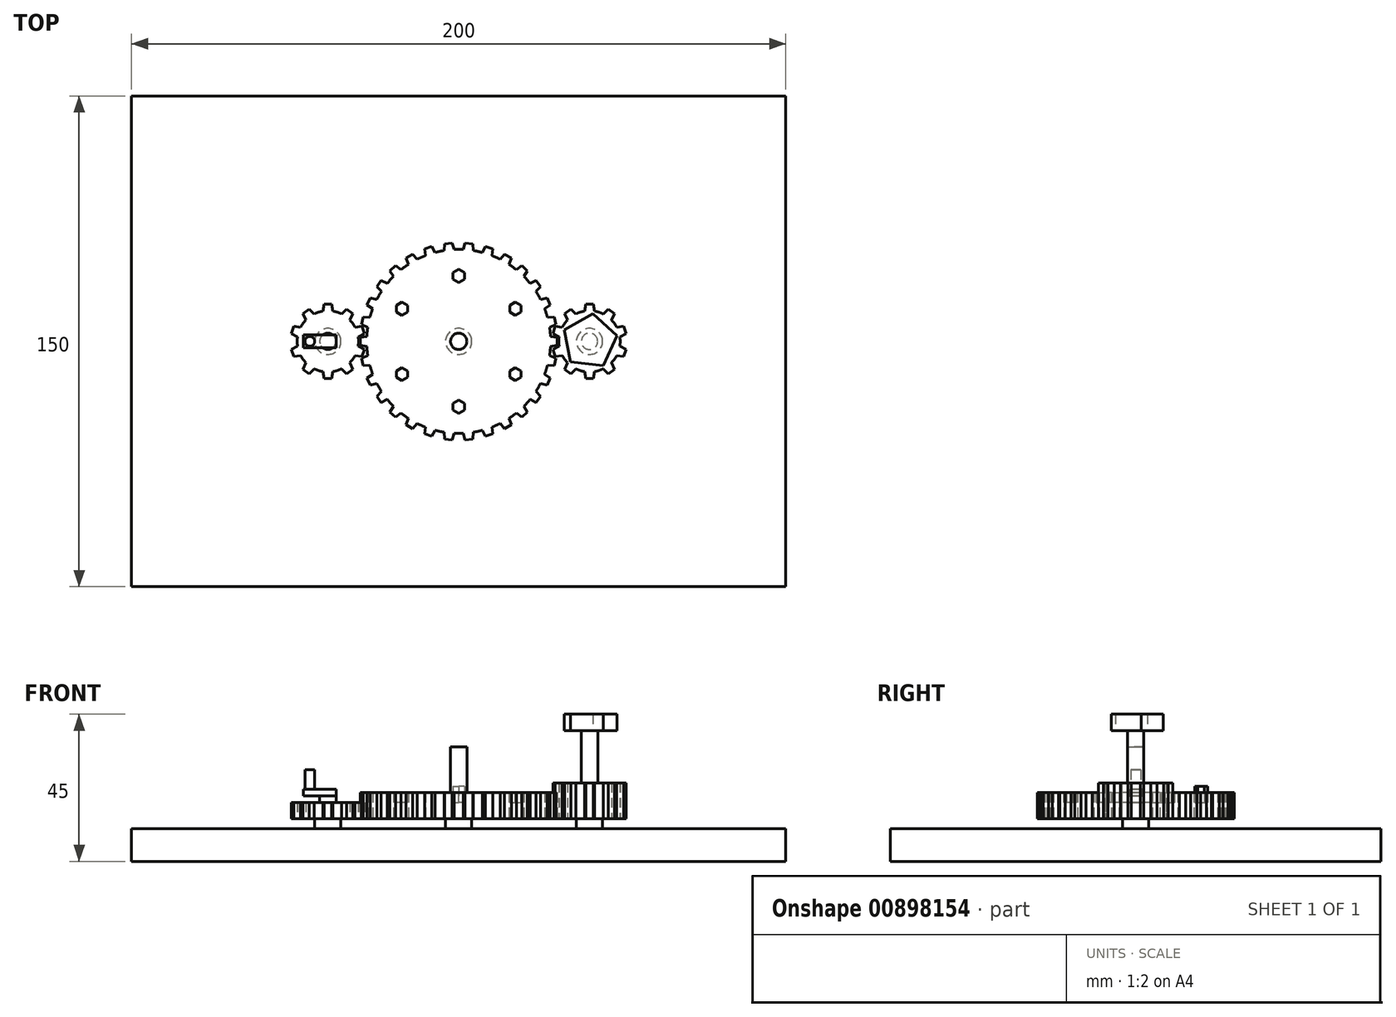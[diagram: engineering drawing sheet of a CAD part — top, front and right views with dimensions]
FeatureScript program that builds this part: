
annotation { "Feature Type Name" : "Feature", "Feature Type Description" : "" }
export const myFeature = defineFeature(function(context is Context, id is Id, definition is map)
    precondition{}
    {
        {
            var Q0;
            Q0=qCreatedBy(makeId("Top.planeOp"),FACE);
            var sketch = newSketch(context, id + "F0", { "sketchPlane" : qUnion([Q0])});
            skLineSegment(sketch, "E0.bottom", {"start": v(-100, 75) * mm, "end": v(100, 75) * mm});
            skLineSegment(sketch, "E0.top", {"start": v(-100, -75) * mm, "end": v(100, -75) * mm});
            skLineSegment(sketch, "E0.left", {"start": v(-100, 75) * mm, "end": v(-100, -75) * mm});
            skLineSegment(sketch, "E0.right", {"start": v(100, 75) * mm, "end": v(100, -75) * mm});
            skPoint(sketch, "E0.middle", {"position": v(0, 0) * mm});
            skSolve(sketch);
        }
        {
            var Q0;
            Q0 = qSketchRegion(id + "F0", true);
            extrude(context, id + "F1", {"entities" : qUnion([Q0]), "depth" : 10 * mm, "offsetDistance" : 25 * mm});
        }
        {
            var Q0;
            Q0=makeQuery(id+"F1.opExtrude","CAP_FACE",FACE,{"disambiguationData":[OSD([sQuery(id+"F0.wireOp",EDGE,"E0.bottom"),sQuery(id+"F0.wireOp",EDGE,"E0.top"),sQuery(id+"F0.wireOp",EDGE,"E0.left"),sQuery(id+"F0.wireOp",EDGE,"E0.right")])],"isStart":false});
            var sketch = newSketch(context, id + "F2", { "sketchPlane" : qUnion([Q0])});
            skCircle(sketch, "E1", {"center": v(0, 0) * mm, "radius": 4 * mm});
            skCircle(sketch, "E2", {"center": v(0, 0) * mm, "radius": 2.5 * mm});
            skCircle(sketch, "E3", {"center": v(-40, 0) * mm, "radius": 4 * mm});
            skCircle(sketch, "E4", {"center": v(-40, 0) * mm, "radius": 2.5 * mm});
            skCircle(sketch, "E5", {"center": v(40, 0) * mm, "radius": 2.5 * mm});
            skCircle(sketch, "E6", {"center": v(40, 0) * mm, "radius": 4 * mm});
            skSolve(sketch);
        }
        {
            var Q0;
            Q0 = qSketchRegion(id + "F2", true);
            extrude(context, id + "F3", {"entities" : qUnion([Q0]), "operationType" : NewBodyOperationType.ADD, "depth" : 3 * mm, "offsetDistance" : 25 * mm});
        }
        {
            var Q0;
            Q0=makeQuery(id+"F3.boolean.opBoolean","SPLIT",FACE,{"disambiguationData":[TD([makeQuery(id+"F3.opExtrude","SWEPT_FACE",FACE,{"disambiguationData":[OSD([sQuery(id+"F2.wireOp",EDGE,"E4")])]})])],"derivedFrom":makeQuery(id+"F1.opExtrude","CAP_FACE",FACE,{"disambiguationData":[OSD([sQuery(id+"F0.wireOp",EDGE,"E0.bottom"),sQuery(id+"F0.wireOp",EDGE,"E0.top"),sQuery(id+"F0.wireOp",EDGE,"E0.left"),sQuery(id+"F0.wireOp",EDGE,"E0.right")])],"isStart":false})});
            extrude(context, id + "F4", {"entities" : qUnion([Q0]), "depth" : 10 * mm, "offsetDistance" : 25 * mm});
        }
        {
            var Q0;
            Q0=makeQuery(id+"F3.opExtrude","CAP_FACE",FACE,{"disambiguationData":[OSD([sQuery(id+"F2.wireOp",EDGE,"E3"),sQuery(id+"F2.wireOp",EDGE,"E4")])],"isStart":false});
            var sketch = newSketch(context, id + "F5", { "sketchPlane" : qUnion([Q0])});
            skCircle(sketch, "E7", {"center": v(-40, 0) * mm, "radius": 9.38 * mm});
            skLineSegment(sketch, "E8", {"start": v(-40, 0) * mm, "end": v(-40, 9.38) * mm, "construction": true});
            skLineSegment(sketch, "E9", {"start": v(-41.55, 9.25) * mm, "end": v(-41.18, 11.37) * mm});
            skLineSegment(sketch, "E10", {"start": v(-41.18, 11.38) * mm, "end": v(-40, 11.38) * mm});
            skLineSegment(sketch, "E11.MirrorCS", {"start": v(-38.82, 11.38) * mm, "end": v(-40, 11.38) * mm});
            skLineSegment(sketch, "E12.MirrorCS", {"start": v(-38.45, 9.25) * mm, "end": v(-38.82, 11.37) * mm});
            skLineSegment(sketch, "E13.1.0", {"start": v(-46.7, 6.57) * mm, "end": v(-47.64, 8.51) * mm});
            skLineSegment(sketch, "E13.1.1", {"start": v(-47.64, 8.51) * mm, "end": v(-46.69, 9.2) * mm});
            skLineSegment(sketch, "E13.1.2", {"start": v(-45.73, 9.9) * mm, "end": v(-46.69, 9.2) * mm});
            skLineSegment(sketch, "E13.1.3", {"start": v(-44.18, 8.4) * mm, "end": v(-45.73, 9.9) * mm});
            skLineSegment(sketch, "E13.2.0", {"start": v(-49.27, 1.38) * mm, "end": v(-51.18, 2.4) * mm});
            skLineSegment(sketch, "E13.2.1", {"start": v(-51.18, 2.4) * mm, "end": v(-50.82, 3.52) * mm});
            skLineSegment(sketch, "E13.2.2", {"start": v(-50.45, 4.64) * mm, "end": v(-50.82, 3.52) * mm});
            skLineSegment(sketch, "E13.2.3", {"start": v(-48.31, 4.33) * mm, "end": v(-50.45, 4.64) * mm});
            skLineSegment(sketch, "E14.1.3.0", {"start": v(-48.31, -4.33) * mm, "end": v(-50.45, -4.64) * mm});
            skLineSegment(sketch, "E14.3.3.0", {"start": v(-50.45, -4.64) * mm, "end": v(-50.82, -3.52) * mm});
            skLineSegment(sketch, "E14.6.3.0", {"start": v(-51.18, -2.4) * mm, "end": v(-50.82, -3.52) * mm});
            skLineSegment(sketch, "E14.9.3.0", {"start": v(-49.27, -1.38) * mm, "end": v(-51.18, -2.4) * mm});
            skLineSegment(sketch, "E14.1.4.0", {"start": v(-44.18, -8.4) * mm, "end": v(-45.73, -9.9) * mm});
            skLineSegment(sketch, "E14.3.4.0", {"start": v(-45.73, -9.9) * mm, "end": v(-46.69, -9.2) * mm});
            skLineSegment(sketch, "E14.6.4.0", {"start": v(-47.64, -8.51) * mm, "end": v(-46.69, -9.2) * mm});
            skLineSegment(sketch, "E14.9.4.0", {"start": v(-46.7, -6.57) * mm, "end": v(-47.64, -8.51) * mm});
            skLineSegment(sketch, "E14.1.5.0", {"start": v(-38.45, -9.25) * mm, "end": v(-38.82, -11.38) * mm});
            skLineSegment(sketch, "E14.3.5.0", {"start": v(-38.82, -11.38) * mm, "end": v(-40, -11.38) * mm});
            skLineSegment(sketch, "E14.6.5.0", {"start": v(-41.18, -11.38) * mm, "end": v(-40, -11.38) * mm});
            skLineSegment(sketch, "E14.9.5.0", {"start": v(-41.55, -9.25) * mm, "end": v(-41.18, -11.38) * mm});
            skLineSegment(sketch, "E14.1.6.0", {"start": v(-33.3, -6.57) * mm, "end": v(-32.36, -8.51) * mm});
            skLineSegment(sketch, "E14.3.6.0", {"start": v(-32.36, -8.51) * mm, "end": v(-33.31, -9.2) * mm});
            skLineSegment(sketch, "E14.6.6.0", {"start": v(-34.27, -9.9) * mm, "end": v(-33.31, -9.2) * mm});
            skLineSegment(sketch, "E14.9.6.0", {"start": v(-35.82, -8.4) * mm, "end": v(-34.27, -9.9) * mm});
            skLineSegment(sketch, "E15.1.7.0", {"start": v(-30.73, -1.38) * mm, "end": v(-28.82, -2.4) * mm});
            skLineSegment(sketch, "E15.3.7.0", {"start": v(-28.82, -2.4) * mm, "end": v(-29.18, -3.52) * mm});
            skLineSegment(sketch, "E15.6.7.0", {"start": v(-29.55, -4.64) * mm, "end": v(-29.18, -3.52) * mm});
            skLineSegment(sketch, "E15.9.7.0", {"start": v(-31.69, -4.33) * mm, "end": v(-29.55, -4.64) * mm});
            skLineSegment(sketch, "E15.1.8.0", {"start": v(-31.69, 4.33) * mm, "end": v(-29.55, 4.64) * mm});
            skLineSegment(sketch, "E15.3.8.0", {"start": v(-29.55, 4.64) * mm, "end": v(-29.18, 3.52) * mm});
            skLineSegment(sketch, "E15.6.8.0", {"start": v(-28.82, 2.4) * mm, "end": v(-29.18, 3.52) * mm});
            skLineSegment(sketch, "E15.9.8.0", {"start": v(-30.73, 1.38) * mm, "end": v(-28.82, 2.4) * mm});
            skLineSegment(sketch, "E16.1.9.0", {"start": v(-35.82, 8.4) * mm, "end": v(-34.27, 9.9) * mm});
            skLineSegment(sketch, "E16.3.9.0", {"start": v(-34.27, 9.9) * mm, "end": v(-33.31, 9.2) * mm});
            skLineSegment(sketch, "E16.6.9.0", {"start": v(-32.36, 8.51) * mm, "end": v(-33.31, 9.2) * mm});
            skLineSegment(sketch, "E16.9.9.0", {"start": v(-33.3, 6.57) * mm, "end": v(-32.36, 8.51) * mm});
            skSolve(sketch);
        }
        {
            var Q0;
            Q0 = qSketchRegion(id + "F5", true);
            extrude(context, id + "F6", {"entities" : qUnion([Q0]), "operationType" : NewBodyOperationType.ADD, "depth" : 5 * mm, "offsetDistance" : 25 * mm});
        }
        {
            var Q0;
            Q0=makeQuery(id+"F3.boolean.opBoolean","SPLIT",FACE,{"disambiguationData":[TD([makeQuery(id+"F3.opExtrude","SWEPT_FACE",FACE,{"disambiguationData":[OSD([sQuery(id+"F2.wireOp",EDGE,"E2")])]})])],"derivedFrom":makeQuery(id+"F1.opExtrude","CAP_FACE",FACE,{"disambiguationData":[OSD([sQuery(id+"F0.wireOp",EDGE,"E0.bottom"),sQuery(id+"F0.wireOp",EDGE,"E0.top"),sQuery(id+"F0.wireOp",EDGE,"E0.left"),sQuery(id+"F0.wireOp",EDGE,"E0.right")])],"isStart":false})});
            extrude(context, id + "F7", {"entities" : qUnion([Q0]), "depth" : 25 * mm, "offsetDistance" : 25 * mm});
        }
        {
            var Q0;
            Q0=makeQuery(id+"F3.boolean.opBoolean","SPLIT",FACE,{"disambiguationData":[TD([makeQuery(id+"F3.opExtrude","SWEPT_FACE",FACE,{"disambiguationData":[OSD([sQuery(id+"F2.wireOp",EDGE,"E5")])]})])],"derivedFrom":makeQuery(id+"F1.opExtrude","CAP_FACE",FACE,{"disambiguationData":[OSD([sQuery(id+"F0.wireOp",EDGE,"E0.bottom"),sQuery(id+"F0.wireOp",EDGE,"E0.top"),sQuery(id+"F0.wireOp",EDGE,"E0.left"),sQuery(id+"F0.wireOp",EDGE,"E0.right")])],"isStart":false})});
            extrude(context, id + "F8", {"entities" : qUnion([Q0]), "depth" : 30 * mm, "offsetDistance" : 25 * mm});
        }
        {
            var Q0;
            Q0=makeQuery(id+"F3.opExtrude","CAP_FACE",FACE,{"disambiguationData":[OSD([sQuery(id+"F2.wireOp",EDGE,"E5"),sQuery(id+"F2.wireOp",EDGE,"E6")])],"isStart":false});
            var sketch = newSketch(context, id + "F9", { "sketchPlane" : qUnion([Q0])});
            skCircle(sketch, "E17", {"center": v(40, 0) * mm, "radius": 9.38 * mm});
            skLineSegment(sketch, "E18", {"start": v(40, 0) * mm, "end": v(40, 9.38) * mm, "construction": true});
            skLineSegment(sketch, "E19", {"start": v(38.45, 9.25) * mm, "end": v(38.82, 11.37) * mm});
            skLineSegment(sketch, "E20", {"start": v(38.82, 11.38) * mm, "end": v(40, 11.38) * mm});
            skLineSegment(sketch, "E21.MirrorCS", {"start": v(41.18, 11.38) * mm, "end": v(40, 11.38) * mm});
            skLineSegment(sketch, "E22.MirrorCS", {"start": v(41.55, 9.25) * mm, "end": v(41.18, 11.37) * mm});
            skLineSegment(sketch, "E23.1.0", {"start": v(33.3, 6.57) * mm, "end": v(32.36, 8.51) * mm});
            skLineSegment(sketch, "E23.1.1", {"start": v(32.36, 8.51) * mm, "end": v(33.31, 9.2) * mm});
            skLineSegment(sketch, "E23.1.2", {"start": v(34.27, 9.9) * mm, "end": v(33.31, 9.2) * mm});
            skLineSegment(sketch, "E23.1.3", {"start": v(35.82, 8.4) * mm, "end": v(34.27, 9.9) * mm});
            skLineSegment(sketch, "E23.2.0", {"start": v(30.73, 1.38) * mm, "end": v(28.82, 2.4) * mm});
            skLineSegment(sketch, "E23.2.1", {"start": v(28.82, 2.4) * mm, "end": v(29.18, 3.52) * mm});
            skLineSegment(sketch, "E23.2.2", {"start": v(29.55, 4.64) * mm, "end": v(29.18, 3.52) * mm});
            skLineSegment(sketch, "E23.2.3", {"start": v(31.69, 4.33) * mm, "end": v(29.55, 4.64) * mm});
            skLineSegment(sketch, "E24.1.3.0", {"start": v(31.69, -4.33) * mm, "end": v(29.55, -4.64) * mm});
            skLineSegment(sketch, "E24.3.3.0", {"start": v(29.55, -4.64) * mm, "end": v(29.18, -3.52) * mm});
            skLineSegment(sketch, "E24.6.3.0", {"start": v(28.82, -2.4) * mm, "end": v(29.18, -3.52) * mm});
            skLineSegment(sketch, "E24.9.3.0", {"start": v(30.73, -1.38) * mm, "end": v(28.82, -2.4) * mm});
            skLineSegment(sketch, "E24.1.4.0", {"start": v(35.82, -8.4) * mm, "end": v(34.27, -9.9) * mm});
            skLineSegment(sketch, "E24.3.4.0", {"start": v(34.27, -9.9) * mm, "end": v(33.31, -9.2) * mm});
            skLineSegment(sketch, "E24.6.4.0", {"start": v(32.36, -8.51) * mm, "end": v(33.31, -9.2) * mm});
            skLineSegment(sketch, "E24.9.4.0", {"start": v(33.3, -6.57) * mm, "end": v(32.36, -8.51) * mm});
            skLineSegment(sketch, "E24.1.5.0", {"start": v(41.55, -9.25) * mm, "end": v(41.18, -11.38) * mm});
            skLineSegment(sketch, "E24.3.5.0", {"start": v(41.18, -11.38) * mm, "end": v(40, -11.38) * mm});
            skLineSegment(sketch, "E24.6.5.0", {"start": v(38.82, -11.38) * mm, "end": v(40, -11.38) * mm});
            skLineSegment(sketch, "E24.9.5.0", {"start": v(38.45, -9.25) * mm, "end": v(38.82, -11.38) * mm});
            skLineSegment(sketch, "E24.1.6.0", {"start": v(46.7, -6.57) * mm, "end": v(47.64, -8.51) * mm});
            skLineSegment(sketch, "E24.3.6.0", {"start": v(47.64, -8.51) * mm, "end": v(46.69, -9.2) * mm});
            skLineSegment(sketch, "E24.6.6.0", {"start": v(45.73, -9.9) * mm, "end": v(46.69, -9.2) * mm});
            skLineSegment(sketch, "E24.9.6.0", {"start": v(44.18, -8.4) * mm, "end": v(45.73, -9.9) * mm});
            skLineSegment(sketch, "E24.1.7.0", {"start": v(49.27, -1.38) * mm, "end": v(51.18, -2.4) * mm});
            skLineSegment(sketch, "E24.3.7.0", {"start": v(51.18, -2.4) * mm, "end": v(50.82, -3.52) * mm});
            skLineSegment(sketch, "E24.6.7.0", {"start": v(50.45, -4.64) * mm, "end": v(50.82, -3.52) * mm});
            skLineSegment(sketch, "E24.9.7.0", {"start": v(48.31, -4.33) * mm, "end": v(50.45, -4.64) * mm});
            skLineSegment(sketch, "E24.1.8.0", {"start": v(48.31, 4.33) * mm, "end": v(50.45, 4.64) * mm});
            skLineSegment(sketch, "E24.3.8.0", {"start": v(50.45, 4.64) * mm, "end": v(50.82, 3.52) * mm});
            skLineSegment(sketch, "E24.6.8.0", {"start": v(51.18, 2.4) * mm, "end": v(50.82, 3.52) * mm});
            skLineSegment(sketch, "E24.9.8.0", {"start": v(49.27, 1.38) * mm, "end": v(51.18, 2.4) * mm});
            skLineSegment(sketch, "E25.1.9.0", {"start": v(44.18, 8.4) * mm, "end": v(45.73, 9.9) * mm});
            skLineSegment(sketch, "E25.3.9.0", {"start": v(45.73, 9.9) * mm, "end": v(46.69, 9.2) * mm});
            skLineSegment(sketch, "E25.6.9.0", {"start": v(47.64, 8.51) * mm, "end": v(46.69, 9.2) * mm});
            skLineSegment(sketch, "E25.9.9.0", {"start": v(46.7, 6.57) * mm, "end": v(47.64, 8.51) * mm});
            skSolve(sketch);
        }
        {
            var Q0;
            Q0 = qSketchRegion(id + "F9", true);
            extrude(context, id + "F10", {"entities" : qUnion([Q0]), "operationType" : NewBodyOperationType.ADD, "depth" : 11 * mm, "offsetDistance" : 25 * mm});
        }
        {
            var Q0;
            Q0=makeQuery(id+"F4.opExtrude","CAP_FACE",FACE,{"disambiguationData":[OSD([sQuery(id+"F0.wireOp",EDGE,"E0.bottom"),sQuery(id+"F0.wireOp",EDGE,"E0.top"),sQuery(id+"F0.wireOp",EDGE,"E0.left"),sQuery(id+"F0.wireOp",EDGE,"E0.right")])],"isStart":false});
            var sketch = newSketch(context, id + "F11", { "sketchPlane" : qUnion([Q0])});
            skLineSegment(sketch, "E26.bottom", {"start": v(-37.5, 2) * mm, "end": v(-47.5, 2) * mm});
            skLineSegment(sketch, "E26.top", {"start": v(-37.5, -2) * mm, "end": v(-47.5, -2) * mm});
            skLineSegment(sketch, "E26.left", {"start": v(-37.5, 2) * mm, "end": v(-37.5, -2) * mm});
            skLineSegment(sketch, "E26.right", {"start": v(-47.5, 2) * mm, "end": v(-47.5, -2) * mm});
            skSolve(sketch);
        }
        {
            var Q0;
            Q0 = qSketchRegion(id + "F11", true);
            extrude(context, id + "F12", {"entities" : qUnion([Q0]), "operationType" : NewBodyOperationType.ADD, "depth" : 2 * mm, "offsetDistance" : 25 * mm});
        }
        {
            var Q0;
            Q0=makeQuery(id+"F12.opExtrude","CAP_FACE",FACE,{"disambiguationData":[OSD([sQuery(id+"F11.wireOp",EDGE,"E26.bottom"),sQuery(id+"F11.wireOp",EDGE,"E26.top"),sQuery(id+"F11.wireOp",EDGE,"E26.left"),sQuery(id+"F11.wireOp",EDGE,"E26.right")])],"isStart":false});
            var sketch = newSketch(context, id + "F13", { "sketchPlane" : qUnion([Q0])});
            skCircle(sketch, "E27", {"center": v(-45.5, 0) * mm, "radius": 1.5 * mm});
            skSolve(sketch);
        }
        {
            var Q0;
            Q0 = qSketchRegion(id + "F13", true);
            extrude(context, id + "F14", {"entities" : qUnion([Q0]), "operationType" : NewBodyOperationType.ADD, "depth" : 6 * mm, "offsetDistance" : 25 * mm});
        }
        {
            var Q0;
            Q0=makeQuery(id+"F8.opExtrude","CAP_FACE",FACE,{"disambiguationData":[OSD([sQuery(id+"F0.wireOp",EDGE,"E0.bottom"),sQuery(id+"F0.wireOp",EDGE,"E0.top"),sQuery(id+"F0.wireOp",EDGE,"E0.left"),sQuery(id+"F0.wireOp",EDGE,"E0.right")])],"isStart":false});
            var sketch = newSketch(context, id + "F15", { "sketchPlane" : qUnion([Q0])});
            skCircle(sketch, "E28.cCircle", {"center": v(40, 0) * mm, "radius": 6.88 * mm, "construction": true});
            skLineSegment(sketch, "E28.0", {"start": v(32.27, 3.55) * mm, "end": v(40.99, 8.45) * mm});
            skLineSegment(sketch, "E28.1", {"start": v(40.99, 8.45) * mm, "end": v(48.34, 1.67) * mm});
            skLineSegment(sketch, "E28.2", {"start": v(48.34, 1.67) * mm, "end": v(44.17, -7.42) * mm});
            skLineSegment(sketch, "E28.3", {"start": v(44.17, -7.42) * mm, "end": v(34.23, -6.25) * mm});
            skLineSegment(sketch, "E28.4", {"start": v(34.23, -6.25) * mm, "end": v(32.27, 3.55) * mm});
            skPoint(sketch, "E28.0.midPoint", {"position": v(36.63, 6) * mm});
            skSolve(sketch);
        }
        {
            var Q0;
            Q0 = qSketchRegion(id + "F15", true);
            extrude(context, id + "F16", {"entities" : qUnion([Q0]), "operationType" : NewBodyOperationType.ADD, "depth" : 5 * mm, "offsetDistance" : 25 * mm});
        }
        {
            var Q0;
            Q0=makeQuery(id+"F3.opExtrude","CAP_FACE",FACE,{"disambiguationData":[OSD([sQuery(id+"F2.wireOp",EDGE,"E1"),sQuery(id+"F2.wireOp",EDGE,"E2")])],"isStart":false});
            var sketch = newSketch(context, id + "F17", { "sketchPlane" : qUnion([Q0])});
            skCircle(sketch, "E29", {"center": v(0, 0) * mm, "radius": 28.12 * mm});
            skLineSegment(sketch, "E30", {"start": v(-30.12, 0) * mm, "end": v(-30.12, -1.18) * mm});
            skLineSegment(sketch, "E31", {"start": v(-30.12, -1.18) * mm, "end": v(-28.08, -1.54) * mm});
            skLineSegment(sketch, "E32.MirrorCS", {"start": v(-30.12, 0) * mm, "end": v(-30.12, 1.18) * mm});
            skLineSegment(sketch, "E33.MirrorCS", {"start": v(-30.12, 1.18) * mm, "end": v(-28.08, 1.54) * mm});
            skLineSegment(sketch, "E34.1.0", {"start": v(-29.71, -5.11) * mm, "end": v(-27.79, -4.33) * mm});
            skLineSegment(sketch, "E34.1.1", {"start": v(-29.47, -6.26) * mm, "end": v(-29.71, -5.11) * mm});
            skLineSegment(sketch, "E34.1.2", {"start": v(-29.47, -6.26) * mm, "end": v(-29.22, -7.42) * mm});
            skLineSegment(sketch, "E34.1.3", {"start": v(-29.22, -7.42) * mm, "end": v(-27.15, -7.34) * mm});
            skLineSegment(sketch, "E34.2.0", {"start": v(-28, -11.18) * mm, "end": v(-26.28, -10.02) * mm});
            skLineSegment(sketch, "E34.2.1", {"start": v(-27.52, -12.25) * mm, "end": v(-28, -11.18) * mm});
            skLineSegment(sketch, "E34.2.2", {"start": v(-27.52, -12.25) * mm, "end": v(-27.04, -13.33) * mm});
            skLineSegment(sketch, "E34.2.3", {"start": v(-27.04, -13.33) * mm, "end": v(-25.03, -12.83) * mm});
            skLineSegment(sketch, "E35.1.3.0", {"start": v(-25.06, -16.75) * mm, "end": v(-23.62, -15.26) * mm});
            skLineSegment(sketch, "E35.3.3.0", {"start": v(-24.37, -17.7) * mm, "end": v(-25.06, -16.75) * mm});
            skLineSegment(sketch, "E35.6.3.0", {"start": v(-24.37, -17.7) * mm, "end": v(-23.68, -18.66) * mm});
            skLineSegment(sketch, "E35.9.3.0", {"start": v(-23.68, -18.66) * mm, "end": v(-21.82, -17.75) * mm});
            skLineSegment(sketch, "E35.1.4.0", {"start": v(-21.03, -21.6) * mm, "end": v(-19.93, -19.84) * mm});
            skLineSegment(sketch, "E35.3.4.0", {"start": v(-20.16, -22.39) * mm, "end": v(-21.03, -21.6) * mm});
            skLineSegment(sketch, "E35.6.4.0", {"start": v(-20.16, -22.39) * mm, "end": v(-19.28, -23.18) * mm});
            skLineSegment(sketch, "E35.9.4.0", {"start": v(-19.28, -23.18) * mm, "end": v(-17.65, -21.9) * mm});
            skLineSegment(sketch, "E35.1.5.0", {"start": v(-16.08, -25.5) * mm, "end": v(-15.37, -23.55) * mm});
            skLineSegment(sketch, "E35.3.5.0", {"start": v(-15.06, -26.09) * mm, "end": v(-16.08, -25.5) * mm});
            skLineSegment(sketch, "E35.6.5.0", {"start": v(-15.06, -26.09) * mm, "end": v(-14.04, -26.68) * mm});
            skLineSegment(sketch, "E35.9.5.0", {"start": v(-14.04, -26.68) * mm, "end": v(-12.7, -25.09) * mm});
            skLineSegment(sketch, "E35.1.6.0", {"start": v(-10.43, -28.29) * mm, "end": v(-10.14, -26.23) * mm});
            skLineSegment(sketch, "E35.3.6.0", {"start": v(-9.3, -28.65) * mm, "end": v(-10.43, -28.29) * mm});
            skLineSegment(sketch, "E35.6.6.0", {"start": v(-9.3, -28.65) * mm, "end": v(-8.19, -29.01) * mm});
            skLineSegment(sketch, "E35.9.6.0", {"start": v(-8.19, -29.01) * mm, "end": v(-7.22, -27.18) * mm});
            skLineSegment(sketch, "E35.1.7.0", {"start": v(-4.32, -29.84) * mm, "end": v(-4.47, -27.77) * mm});
            skLineSegment(sketch, "E35.3.7.0", {"start": v(-3.15, -29.96) * mm, "end": v(-4.32, -29.84) * mm});
            skLineSegment(sketch, "E35.6.7.0", {"start": v(-3.15, -29.96) * mm, "end": v(-1.98, -30.08) * mm});
            skLineSegment(sketch, "E35.9.7.0", {"start": v(-1.98, -30.08) * mm, "end": v(-1.4, -28.09) * mm});
            skLineSegment(sketch, "E35.1.8.0", {"start": v(1.98, -30.08) * mm, "end": v(1.4, -28.09) * mm});
            skLineSegment(sketch, "E35.3.8.0", {"start": v(3.15, -29.96) * mm, "end": v(1.98, -30.08) * mm});
            skLineSegment(sketch, "E35.6.8.0", {"start": v(3.15, -29.96) * mm, "end": v(4.32, -29.84) * mm});
            skLineSegment(sketch, "E35.9.8.0", {"start": v(4.32, -29.84) * mm, "end": v(4.47, -27.77) * mm});
            skLineSegment(sketch, "E35.1.9.0", {"start": v(8.19, -29.01) * mm, "end": v(7.22, -27.18) * mm});
            skLineSegment(sketch, "E35.3.9.0", {"start": v(9.3, -28.65) * mm, "end": v(8.19, -29.01) * mm});
            skLineSegment(sketch, "E35.6.9.0", {"start": v(9.3, -28.65) * mm, "end": v(10.43, -28.29) * mm});
            skLineSegment(sketch, "E35.9.9.0", {"start": v(10.43, -28.29) * mm, "end": v(10.14, -26.23) * mm});
            skLineSegment(sketch, "E35.1.10.0", {"start": v(14.04, -26.68) * mm, "end": v(12.7, -25.09) * mm});
            skLineSegment(sketch, "E35.3.10.0", {"start": v(15.06, -26.09) * mm, "end": v(14.04, -26.68) * mm});
            skLineSegment(sketch, "E35.6.10.0", {"start": v(15.06, -26.09) * mm, "end": v(16.08, -25.5) * mm});
            skLineSegment(sketch, "E35.9.10.0", {"start": v(16.08, -25.5) * mm, "end": v(15.37, -23.55) * mm});
            skLineSegment(sketch, "E35.1.11.0", {"start": v(19.28, -23.18) * mm, "end": v(17.65, -21.9) * mm});
            skLineSegment(sketch, "E35.3.11.0", {"start": v(20.16, -22.39) * mm, "end": v(19.28, -23.18) * mm});
            skLineSegment(sketch, "E35.6.11.0", {"start": v(20.16, -22.39) * mm, "end": v(21.03, -21.6) * mm});
            skLineSegment(sketch, "E35.9.11.0", {"start": v(21.03, -21.6) * mm, "end": v(19.93, -19.84) * mm});
            skLineSegment(sketch, "E35.1.12.0", {"start": v(23.68, -18.66) * mm, "end": v(21.82, -17.75) * mm});
            skLineSegment(sketch, "E35.3.12.0", {"start": v(24.37, -17.7) * mm, "end": v(23.68, -18.66) * mm});
            skLineSegment(sketch, "E35.6.12.0", {"start": v(24.37, -17.7) * mm, "end": v(25.06, -16.75) * mm});
            skLineSegment(sketch, "E35.9.12.0", {"start": v(25.06, -16.75) * mm, "end": v(23.62, -15.26) * mm});
            skLineSegment(sketch, "E35.1.13.0", {"start": v(27.04, -13.33) * mm, "end": v(25.03, -12.83) * mm});
            skLineSegment(sketch, "E35.3.13.0", {"start": v(27.52, -12.25) * mm, "end": v(27.04, -13.33) * mm});
            skLineSegment(sketch, "E35.6.13.0", {"start": v(27.52, -12.25) * mm, "end": v(28, -11.18) * mm});
            skLineSegment(sketch, "E35.9.13.0", {"start": v(28, -11.18) * mm, "end": v(26.28, -10.02) * mm});
            skLineSegment(sketch, "E35.1.14.0", {"start": v(29.22, -7.42) * mm, "end": v(27.15, -7.34) * mm});
            skLineSegment(sketch, "E35.3.14.0", {"start": v(29.47, -6.26) * mm, "end": v(29.22, -7.42) * mm});
            skLineSegment(sketch, "E35.6.14.0", {"start": v(29.47, -6.26) * mm, "end": v(29.71, -5.11) * mm});
            skLineSegment(sketch, "E35.9.14.0", {"start": v(29.71, -5.11) * mm, "end": v(27.79, -4.33) * mm});
            skLineSegment(sketch, "E35.1.15.0", {"start": v(30.12, -1.18) * mm, "end": v(28.08, -1.54) * mm});
            skLineSegment(sketch, "E35.3.15.0", {"start": v(30.12, 0) * mm, "end": v(30.12, -1.18) * mm});
            skLineSegment(sketch, "E35.6.15.0", {"start": v(30.12, 0) * mm, "end": v(30.12, 1.18) * mm});
            skLineSegment(sketch, "E35.9.15.0", {"start": v(30.12, 1.18) * mm, "end": v(28.08, 1.54) * mm});
            skLineSegment(sketch, "E35.1.16.0", {"start": v(29.71, 5.11) * mm, "end": v(27.79, 4.33) * mm});
            skLineSegment(sketch, "E35.3.16.0", {"start": v(29.47, 6.26) * mm, "end": v(29.71, 5.11) * mm});
            skLineSegment(sketch, "E35.6.16.0", {"start": v(29.47, 6.26) * mm, "end": v(29.22, 7.42) * mm});
            skLineSegment(sketch, "E35.9.16.0", {"start": v(29.22, 7.42) * mm, "end": v(27.15, 7.34) * mm});
            skLineSegment(sketch, "E35.1.17.0", {"start": v(28, 11.18) * mm, "end": v(26.28, 10.02) * mm});
            skLineSegment(sketch, "E35.3.17.0", {"start": v(27.52, 12.25) * mm, "end": v(28, 11.18) * mm});
            skLineSegment(sketch, "E35.6.17.0", {"start": v(27.52, 12.25) * mm, "end": v(27.04, 13.33) * mm});
            skLineSegment(sketch, "E35.9.17.0", {"start": v(27.04, 13.33) * mm, "end": v(25.03, 12.83) * mm});
            skLineSegment(sketch, "E35.1.18.0", {"start": v(25.06, 16.75) * mm, "end": v(23.62, 15.26) * mm});
            skLineSegment(sketch, "E35.3.18.0", {"start": v(24.37, 17.7) * mm, "end": v(25.06, 16.75) * mm});
            skLineSegment(sketch, "E35.6.18.0", {"start": v(24.37, 17.7) * mm, "end": v(23.68, 18.66) * mm});
            skLineSegment(sketch, "E35.9.18.0", {"start": v(23.68, 18.66) * mm, "end": v(21.82, 17.75) * mm});
            skLineSegment(sketch, "E35.1.19.0", {"start": v(21.03, 21.6) * mm, "end": v(19.93, 19.84) * mm});
            skLineSegment(sketch, "E35.3.19.0", {"start": v(20.16, 22.39) * mm, "end": v(21.03, 21.6) * mm});
            skLineSegment(sketch, "E35.6.19.0", {"start": v(20.16, 22.39) * mm, "end": v(19.28, 23.18) * mm});
            skLineSegment(sketch, "E35.9.19.0", {"start": v(19.28, 23.18) * mm, "end": v(17.65, 21.9) * mm});
            skLineSegment(sketch, "E35.1.20.0", {"start": v(16.08, 25.5) * mm, "end": v(15.37, 23.55) * mm});
            skLineSegment(sketch, "E35.3.20.0", {"start": v(15.06, 26.09) * mm, "end": v(16.08, 25.5) * mm});
            skLineSegment(sketch, "E35.6.20.0", {"start": v(15.06, 26.09) * mm, "end": v(14.04, 26.68) * mm});
            skLineSegment(sketch, "E35.9.20.0", {"start": v(14.04, 26.68) * mm, "end": v(12.7, 25.09) * mm});
            skLineSegment(sketch, "E35.1.21.0", {"start": v(10.43, 28.29) * mm, "end": v(10.14, 26.23) * mm});
            skLineSegment(sketch, "E35.3.21.0", {"start": v(9.3, 28.65) * mm, "end": v(10.43, 28.29) * mm});
            skLineSegment(sketch, "E35.6.21.0", {"start": v(9.3, 28.65) * mm, "end": v(8.19, 29.01) * mm});
            skLineSegment(sketch, "E35.9.21.0", {"start": v(8.19, 29.01) * mm, "end": v(7.22, 27.18) * mm});
            skLineSegment(sketch, "E35.1.22.0", {"start": v(4.32, 29.84) * mm, "end": v(4.47, 27.77) * mm});
            skLineSegment(sketch, "E35.3.22.0", {"start": v(3.15, 29.96) * mm, "end": v(4.32, 29.84) * mm});
            skLineSegment(sketch, "E35.6.22.0", {"start": v(3.15, 29.96) * mm, "end": v(1.98, 30.08) * mm});
            skLineSegment(sketch, "E35.9.22.0", {"start": v(1.98, 30.08) * mm, "end": v(1.4, 28.09) * mm});
            skLineSegment(sketch, "E35.1.23.0", {"start": v(-1.98, 30.08) * mm, "end": v(-1.4, 28.09) * mm});
            skLineSegment(sketch, "E35.3.23.0", {"start": v(-3.15, 29.96) * mm, "end": v(-1.98, 30.08) * mm});
            skLineSegment(sketch, "E35.6.23.0", {"start": v(-3.15, 29.96) * mm, "end": v(-4.32, 29.84) * mm});
            skLineSegment(sketch, "E35.9.23.0", {"start": v(-4.32, 29.84) * mm, "end": v(-4.47, 27.77) * mm});
            skLineSegment(sketch, "E35.1.24.0", {"start": v(-8.19, 29.01) * mm, "end": v(-7.22, 27.18) * mm});
            skLineSegment(sketch, "E35.3.24.0", {"start": v(-9.3, 28.65) * mm, "end": v(-8.19, 29.01) * mm});
            skLineSegment(sketch, "E35.6.24.0", {"start": v(-9.3, 28.65) * mm, "end": v(-10.43, 28.29) * mm});
            skLineSegment(sketch, "E35.9.24.0", {"start": v(-10.43, 28.29) * mm, "end": v(-10.14, 26.23) * mm});
            skLineSegment(sketch, "E35.1.25.0", {"start": v(-14.04, 26.68) * mm, "end": v(-12.7, 25.09) * mm});
            skLineSegment(sketch, "E35.3.25.0", {"start": v(-15.06, 26.09) * mm, "end": v(-14.04, 26.68) * mm});
            skLineSegment(sketch, "E35.6.25.0", {"start": v(-15.06, 26.09) * mm, "end": v(-16.08, 25.5) * mm});
            skLineSegment(sketch, "E35.9.25.0", {"start": v(-16.08, 25.5) * mm, "end": v(-15.37, 23.55) * mm});
            skLineSegment(sketch, "E35.1.26.0", {"start": v(-19.28, 23.18) * mm, "end": v(-17.65, 21.9) * mm});
            skLineSegment(sketch, "E35.3.26.0", {"start": v(-20.16, 22.39) * mm, "end": v(-19.28, 23.18) * mm});
            skLineSegment(sketch, "E35.6.26.0", {"start": v(-20.16, 22.39) * mm, "end": v(-21.03, 21.6) * mm});
            skLineSegment(sketch, "E35.9.26.0", {"start": v(-21.03, 21.6) * mm, "end": v(-19.93, 19.84) * mm});
            skLineSegment(sketch, "E35.1.27.0", {"start": v(-23.68, 18.66) * mm, "end": v(-21.82, 17.75) * mm});
            skLineSegment(sketch, "E35.3.27.0", {"start": v(-24.37, 17.7) * mm, "end": v(-23.68, 18.66) * mm});
            skLineSegment(sketch, "E35.6.27.0", {"start": v(-24.37, 17.7) * mm, "end": v(-25.06, 16.75) * mm});
            skLineSegment(sketch, "E35.9.27.0", {"start": v(-25.06, 16.75) * mm, "end": v(-23.62, 15.26) * mm});
            skLineSegment(sketch, "E35.1.28.0", {"start": v(-27.04, 13.33) * mm, "end": v(-25.03, 12.83) * mm});
            skLineSegment(sketch, "E35.3.28.0", {"start": v(-27.52, 12.25) * mm, "end": v(-27.04, 13.33) * mm});
            skLineSegment(sketch, "E35.6.28.0", {"start": v(-27.52, 12.25) * mm, "end": v(-28, 11.18) * mm});
            skLineSegment(sketch, "E35.9.28.0", {"start": v(-28, 11.18) * mm, "end": v(-26.28, 10.02) * mm});
            skLineSegment(sketch, "E35.1.29.0", {"start": v(-29.22, 7.42) * mm, "end": v(-27.15, 7.34) * mm});
            skLineSegment(sketch, "E35.3.29.0", {"start": v(-29.47, 6.26) * mm, "end": v(-29.22, 7.42) * mm});
            skLineSegment(sketch, "E35.6.29.0", {"start": v(-29.47, 6.26) * mm, "end": v(-29.71, 5.11) * mm});
            skLineSegment(sketch, "E35.9.29.0", {"start": v(-29.71, 5.11) * mm, "end": v(-27.79, 4.33) * mm});
            skSolve(sketch);
        }
        {
            var Q0;
            Q0 = qSketchRegion(id + "F17", true);
            extrude(context, id + "F18", {"entities" : qUnion([Q0]), "operationType" : NewBodyOperationType.ADD, "depth" : 8 * mm, "offsetDistance" : 25 * mm});
        }
        {
            var Q0;
            Q0=makeQuery(id+"F18.opExtrude","CAP_FACE",FACE,{"disambiguationData":[OSD([sQuery(id+"F17.wireOp",EDGE,"E29"),sQuery(id+"F17.wireOp",EDGE,"E30"),sQuery(id+"F17.wireOp",EDGE,"E31"),sQuery(id+"F17.wireOp",EDGE,"E32.MirrorCS"),sQuery(id+"F17.wireOp",EDGE,"E33.MirrorCS"),sQuery(id+"F17.wireOp",EDGE,"E34.1.0"),sQuery(id+"F17.wireOp",EDGE,"E34.1.1"),sQuery(id+"F17.wireOp",EDGE,"E34.1.2"),sQuery(id+"F17.wireOp",EDGE,"E34.1.3"),sQuery(id+"F17.wireOp",EDGE,"E34.2.0"),sQuery(id+"F17.wireOp",EDGE,"E34.2.1"),sQuery(id+"F17.wireOp",EDGE,"E34.2.2"),sQuery(id+"F17.wireOp",EDGE,"E34.2.3"),sQuery(id+"F17.wireOp",EDGE,"E35.1.3.0"),sQuery(id+"F17.wireOp",EDGE,"E35.3.3.0"),sQuery(id+"F17.wireOp",EDGE,"E35.6.3.0"),sQuery(id+"F17.wireOp",EDGE,"E35.9.3.0"),sQuery(id+"F17.wireOp",EDGE,"E35.1.4.0"),sQuery(id+"F17.wireOp",EDGE,"E35.3.4.0"),sQuery(id+"F17.wireOp",EDGE,"E35.6.4.0"),sQuery(id+"F17.wireOp",EDGE,"E35.9.4.0"),sQuery(id+"F17.wireOp",EDGE,"E35.1.5.0"),sQuery(id+"F17.wireOp",EDGE,"E35.3.5.0"),sQuery(id+"F17.wireOp",EDGE,"E35.6.5.0"),sQuery(id+"F17.wireOp",EDGE,"E35.9.5.0"),sQuery(id+"F17.wireOp",EDGE,"E35.1.6.0"),sQuery(id+"F17.wireOp",EDGE,"E35.3.6.0"),sQuery(id+"F17.wireOp",EDGE,"E35.6.6.0"),sQuery(id+"F17.wireOp",EDGE,"E35.9.6.0"),sQuery(id+"F17.wireOp",EDGE,"E35.1.7.0"),sQuery(id+"F17.wireOp",EDGE,"E35.3.7.0"),sQuery(id+"F17.wireOp",EDGE,"E35.6.7.0"),sQuery(id+"F17.wireOp",EDGE,"E35.9.7.0"),sQuery(id+"F17.wireOp",EDGE,"E35.1.8.0"),sQuery(id+"F17.wireOp",EDGE,"E35.3.8.0"),sQuery(id+"F17.wireOp",EDGE,"E35.6.8.0"),sQuery(id+"F17.wireOp",EDGE,"E35.9.8.0"),sQuery(id+"F17.wireOp",EDGE,"E35.1.9.0"),sQuery(id+"F17.wireOp",EDGE,"E35.3.9.0"),sQuery(id+"F17.wireOp",EDGE,"E35.6.9.0"),sQuery(id+"F17.wireOp",EDGE,"E35.9.9.0"),sQuery(id+"F17.wireOp",EDGE,"E35.1.10.0"),sQuery(id+"F17.wireOp",EDGE,"E35.3.10.0"),sQuery(id+"F17.wireOp",EDGE,"E35.6.10.0"),sQuery(id+"F17.wireOp",EDGE,"E35.9.10.0"),sQuery(id+"F17.wireOp",EDGE,"E35.1.11.0"),sQuery(id+"F17.wireOp",EDGE,"E35.3.11.0"),sQuery(id+"F17.wireOp",EDGE,"E35.6.11.0"),sQuery(id+"F17.wireOp",EDGE,"E35.9.11.0"),sQuery(id+"F17.wireOp",EDGE,"E35.1.12.0"),sQuery(id+"F17.wireOp",EDGE,"E35.3.12.0"),sQuery(id+"F17.wireOp",EDGE,"E35.6.12.0"),sQuery(id+"F17.wireOp",EDGE,"E35.9.12.0"),sQuery(id+"F17.wireOp",EDGE,"E35.1.13.0"),sQuery(id+"F17.wireOp",EDGE,"E35.3.13.0"),sQuery(id+"F17.wireOp",EDGE,"E35.6.13.0"),sQuery(id+"F17.wireOp",EDGE,"E35.9.13.0"),sQuery(id+"F17.wireOp",EDGE,"E35.1.14.0"),sQuery(id+"F17.wireOp",EDGE,"E35.3.14.0"),sQuery(id+"F17.wireOp",EDGE,"E35.6.14.0"),sQuery(id+"F17.wireOp",EDGE,"E35.9.14.0"),sQuery(id+"F17.wireOp",EDGE,"E35.1.15.0"),sQuery(id+"F17.wireOp",EDGE,"E35.3.15.0"),sQuery(id+"F17.wireOp",EDGE,"E35.6.15.0"),sQuery(id+"F17.wireOp",EDGE,"E35.9.15.0"),sQuery(id+"F17.wireOp",EDGE,"E35.1.16.0"),sQuery(id+"F17.wireOp",EDGE,"E35.3.16.0"),sQuery(id+"F17.wireOp",EDGE,"E35.6.16.0"),sQuery(id+"F17.wireOp",EDGE,"E35.9.16.0"),sQuery(id+"F17.wireOp",EDGE,"E35.1.17.0"),sQuery(id+"F17.wireOp",EDGE,"E35.3.17.0"),sQuery(id+"F17.wireOp",EDGE,"E35.6.17.0"),sQuery(id+"F17.wireOp",EDGE,"E35.9.17.0"),sQuery(id+"F17.wireOp",EDGE,"E35.1.18.0"),sQuery(id+"F17.wireOp",EDGE,"E35.3.18.0"),sQuery(id+"F17.wireOp",EDGE,"E35.6.18.0"),sQuery(id+"F17.wireOp",EDGE,"E35.9.18.0"),sQuery(id+"F17.wireOp",EDGE,"E35.1.19.0"),sQuery(id+"F17.wireOp",EDGE,"E35.3.19.0"),sQuery(id+"F17.wireOp",EDGE,"E35.6.19.0"),sQuery(id+"F17.wireOp",EDGE,"E35.9.19.0"),sQuery(id+"F17.wireOp",EDGE,"E35.1.20.0"),sQuery(id+"F17.wireOp",EDGE,"E35.3.20.0"),sQuery(id+"F17.wireOp",EDGE,"E35.6.20.0"),sQuery(id+"F17.wireOp",EDGE,"E35.9.20.0"),sQuery(id+"F17.wireOp",EDGE,"E35.1.21.0"),sQuery(id+"F17.wireOp",EDGE,"E35.3.21.0"),sQuery(id+"F17.wireOp",EDGE,"E35.6.21.0"),sQuery(id+"F17.wireOp",EDGE,"E35.9.21.0"),sQuery(id+"F17.wireOp",EDGE,"E35.1.22.0"),sQuery(id+"F17.wireOp",EDGE,"E35.3.22.0"),sQuery(id+"F17.wireOp",EDGE,"E35.6.22.0"),sQuery(id+"F17.wireOp",EDGE,"E35.9.22.0"),sQuery(id+"F17.wireOp",EDGE,"E35.1.23.0"),sQuery(id+"F17.wireOp",EDGE,"E35.3.23.0"),sQuery(id+"F17.wireOp",EDGE,"E35.6.23.0"),sQuery(id+"F17.wireOp",EDGE,"E35.9.23.0"),sQuery(id+"F17.wireOp",EDGE,"E35.1.24.0"),sQuery(id+"F17.wireOp",EDGE,"E35.3.24.0"),sQuery(id+"F17.wireOp",EDGE,"E35.6.24.0"),sQuery(id+"F17.wireOp",EDGE,"E35.9.24.0"),sQuery(id+"F17.wireOp",EDGE,"E35.1.25.0"),sQuery(id+"F17.wireOp",EDGE,"E35.3.25.0"),sQuery(id+"F17.wireOp",EDGE,"E35.6.25.0"),sQuery(id+"F17.wireOp",EDGE,"E35.9.25.0"),sQuery(id+"F17.wireOp",EDGE,"E35.1.26.0"),sQuery(id+"F17.wireOp",EDGE,"E35.3.26.0"),sQuery(id+"F17.wireOp",EDGE,"E35.6.26.0"),sQuery(id+"F17.wireOp",EDGE,"E35.9.26.0"),sQuery(id+"F17.wireOp",EDGE,"E35.1.27.0"),sQuery(id+"F17.wireOp",EDGE,"E35.3.27.0"),sQuery(id+"F17.wireOp",EDGE,"E35.6.27.0"),sQuery(id+"F17.wireOp",EDGE,"E35.9.27.0"),sQuery(id+"F17.wireOp",EDGE,"E35.1.28.0"),sQuery(id+"F17.wireOp",EDGE,"E35.3.28.0"),sQuery(id+"F17.wireOp",EDGE,"E35.6.28.0"),sQuery(id+"F17.wireOp",EDGE,"E35.9.28.0"),sQuery(id+"F17.wireOp",EDGE,"E35.1.29.0"),sQuery(id+"F17.wireOp",EDGE,"E35.3.29.0"),sQuery(id+"F17.wireOp",EDGE,"E35.6.29.0"),sQuery(id+"F17.wireOp",EDGE,"E35.9.29.0")])],"isStart":false});
            var sketch = newSketch(context, id + "F19", { "sketchPlane" : qUnion([Q0])});
            skCircle(sketch, "E36.cCircle", {"center": v(0, 20) * mm, "radius": 1.73 * mm, "construction": true});
            skLineSegment(sketch, "E36.0", {"start": v(-1.73, 21) * mm, "end": v(0, 22) * mm});
            skLineSegment(sketch, "E36.1", {"start": v(0, 22) * mm, "end": v(1.73, 21) * mm});
            skLineSegment(sketch, "E36.2", {"start": v(1.73, 21) * mm, "end": v(1.73, 19) * mm});
            skLineSegment(sketch, "E36.3", {"start": v(1.73, 19) * mm, "end": v(0, 18) * mm});
            skLineSegment(sketch, "E36.4", {"start": v(0, 18) * mm, "end": v(-1.73, 19) * mm});
            skLineSegment(sketch, "E36.5", {"start": v(-1.73, 19) * mm, "end": v(-1.73, 21) * mm});
            skPoint(sketch, "E36.0.midPoint", {"position": v(-0.87, 21.5) * mm});
            skLineSegment(sketch, "E37.1.0", {"start": v(-19.05, 9) * mm, "end": v(-19.05, 11) * mm});
            skLineSegment(sketch, "E37.1.1", {"start": v(-19.05, 11) * mm, "end": v(-17.32, 12) * mm});
            skLineSegment(sketch, "E37.1.2", {"start": v(-17.32, 12) * mm, "end": v(-15.59, 11) * mm});
            skLineSegment(sketch, "E37.1.3", {"start": v(-17.32, 8) * mm, "end": v(-19.05, 9) * mm});
            skLineSegment(sketch, "E37.1.4", {"start": v(-15.59, 9) * mm, "end": v(-17.32, 8) * mm});
            skLineSegment(sketch, "E37.1.5", {"start": v(-15.59, 11) * mm, "end": v(-15.59, 9) * mm});
            skLineSegment(sketch, "E37.2.0", {"start": v(-17.32, -12) * mm, "end": v(-19.05, -11) * mm});
            skLineSegment(sketch, "E37.2.1", {"start": v(-19.05, -11) * mm, "end": v(-19.05, -9) * mm});
            skLineSegment(sketch, "E37.2.2", {"start": v(-19.05, -9) * mm, "end": v(-17.32, -8) * mm});
            skLineSegment(sketch, "E37.2.3", {"start": v(-15.59, -11) * mm, "end": v(-17.32, -12) * mm});
            skLineSegment(sketch, "E37.2.4", {"start": v(-15.59, -9) * mm, "end": v(-15.59, -11) * mm});
            skLineSegment(sketch, "E37.2.5", {"start": v(-17.32, -8) * mm, "end": v(-15.59, -9) * mm});
            skLineSegment(sketch, "E37.3.0", {"start": v(1.73, -21) * mm, "end": v(0, -22) * mm});
            skLineSegment(sketch, "E37.3.1", {"start": v(0, -22) * mm, "end": v(-1.73, -21) * mm});
            skLineSegment(sketch, "E37.3.2", {"start": v(-1.73, -21) * mm, "end": v(-1.73, -19) * mm});
            skLineSegment(sketch, "E37.3.3", {"start": v(1.73, -19) * mm, "end": v(1.73, -21) * mm});
            skLineSegment(sketch, "E37.3.4", {"start": v(0, -18) * mm, "end": v(1.73, -19) * mm});
            skLineSegment(sketch, "E37.3.5", {"start": v(-1.73, -19) * mm, "end": v(0, -18) * mm});
            skLineSegment(sketch, "E37.4.0", {"start": v(19.05, -9) * mm, "end": v(19.05, -11) * mm});
            skLineSegment(sketch, "E37.4.1", {"start": v(19.05, -11) * mm, "end": v(17.32, -12) * mm});
            skLineSegment(sketch, "E37.4.2", {"start": v(17.32, -12) * mm, "end": v(15.59, -11) * mm});
            skLineSegment(sketch, "E37.4.3", {"start": v(17.32, -8) * mm, "end": v(19.05, -9) * mm});
            skLineSegment(sketch, "E37.4.4", {"start": v(15.59, -9) * mm, "end": v(17.32, -8) * mm});
            skLineSegment(sketch, "E37.4.5", {"start": v(15.59, -11) * mm, "end": v(15.59, -9) * mm});
            skLineSegment(sketch, "E37.5.0", {"start": v(17.32, 12) * mm, "end": v(19.05, 11) * mm});
            skLineSegment(sketch, "E37.5.1", {"start": v(19.05, 11) * mm, "end": v(19.05, 9) * mm});
            skLineSegment(sketch, "E37.5.2", {"start": v(19.05, 9) * mm, "end": v(17.32, 8) * mm});
            skLineSegment(sketch, "E37.5.3", {"start": v(15.59, 11) * mm, "end": v(17.32, 12) * mm});
            skLineSegment(sketch, "E37.5.4", {"start": v(15.59, 9) * mm, "end": v(15.59, 11) * mm});
            skLineSegment(sketch, "E37.5.5", {"start": v(17.32, 8) * mm, "end": v(15.59, 9) * mm});
            skPoint(sketch, "E37.center", {"position": v(0, 0) * mm});
            skSolve(sketch);
        }
        {
            var Q0;
            Q0=makeQuery(id+"F19.imprint","IMPRINT",FACE,{"disambiguationData":[TD([[makeQuery(id+"F19.imprint","IMPRINT",EDGE,{"derivedFrom":sQuery(id+"F19.wireOp",EDGE,"E36.0")}),-1.0]])]});
            var Q1;
            Q1=makeQuery(id+"F19.imprint","IMPRINT",FACE,{"disambiguationData":[TD([[makeQuery(id+"F19.imprint","IMPRINT",EDGE,{"derivedFrom":sQuery(id+"F19.wireOp",EDGE,"E37.1.0")}),-1.0]])]});
            var Q2;
            Q2=makeQuery(id+"F19.imprint","IMPRINT",FACE,{"disambiguationData":[TD([[makeQuery(id+"F19.imprint","IMPRINT",EDGE,{"derivedFrom":sQuery(id+"F19.wireOp",EDGE,"E37.2.0")}),-1.0]])]});
            var Q3;
            Q3=makeQuery(id+"F19.imprint","IMPRINT",FACE,{"disambiguationData":[TD([[makeQuery(id+"F19.imprint","IMPRINT",EDGE,{"derivedFrom":sQuery(id+"F19.wireOp",EDGE,"E37.3.0")}),-1.0]])]});
            var Q4;
            Q4=makeQuery(id+"F19.imprint","IMPRINT",FACE,{"disambiguationData":[TD([[makeQuery(id+"F19.imprint","IMPRINT",EDGE,{"derivedFrom":sQuery(id+"F19.wireOp",EDGE,"E37.4.0")}),-1.0]])]});
            var Q5;
            Q5=makeQuery(id+"F19.imprint","IMPRINT",FACE,{"disambiguationData":[TD([[makeQuery(id+"F19.imprint","IMPRINT",EDGE,{"derivedFrom":sQuery(id+"F19.wireOp",EDGE,"E37.5.0")}),-1.0]])]});
            extrude(context, id + "F20", {"entities" : qUnion([Q0, Q1, Q2, Q3, Q4, Q5]), "operationType" : NewBodyOperationType.REMOVE, "oppositeDirection" : true, "depth" : 3 * mm, "offsetDistance" : 25 * mm});
        }
        {
            var Q0;
            Q0=makeQuery(id+"F20.boolean.opBoolean","COPY",FACE,{"derivedFrom":makeQuery(id+"F20.opExtrude","CAP_FACE",FACE,{"disambiguationData":[OSD([sQuery(id+"F19.wireOp",EDGE,"E36.0"),sQuery(id+"F19.wireOp",EDGE,"E36.1"),sQuery(id+"F19.wireOp",EDGE,"E36.2"),sQuery(id+"F19.wireOp",EDGE,"E36.3"),sQuery(id+"F19.wireOp",EDGE,"E36.4"),sQuery(id+"F19.wireOp",EDGE,"E36.5")])],"isStart":false})});
            extrude(context, id + "F21", {"entities" : qUnion([Q0]), "depth" : 5 * mm, "offsetDistance" : 25 * mm});
        }
    });
